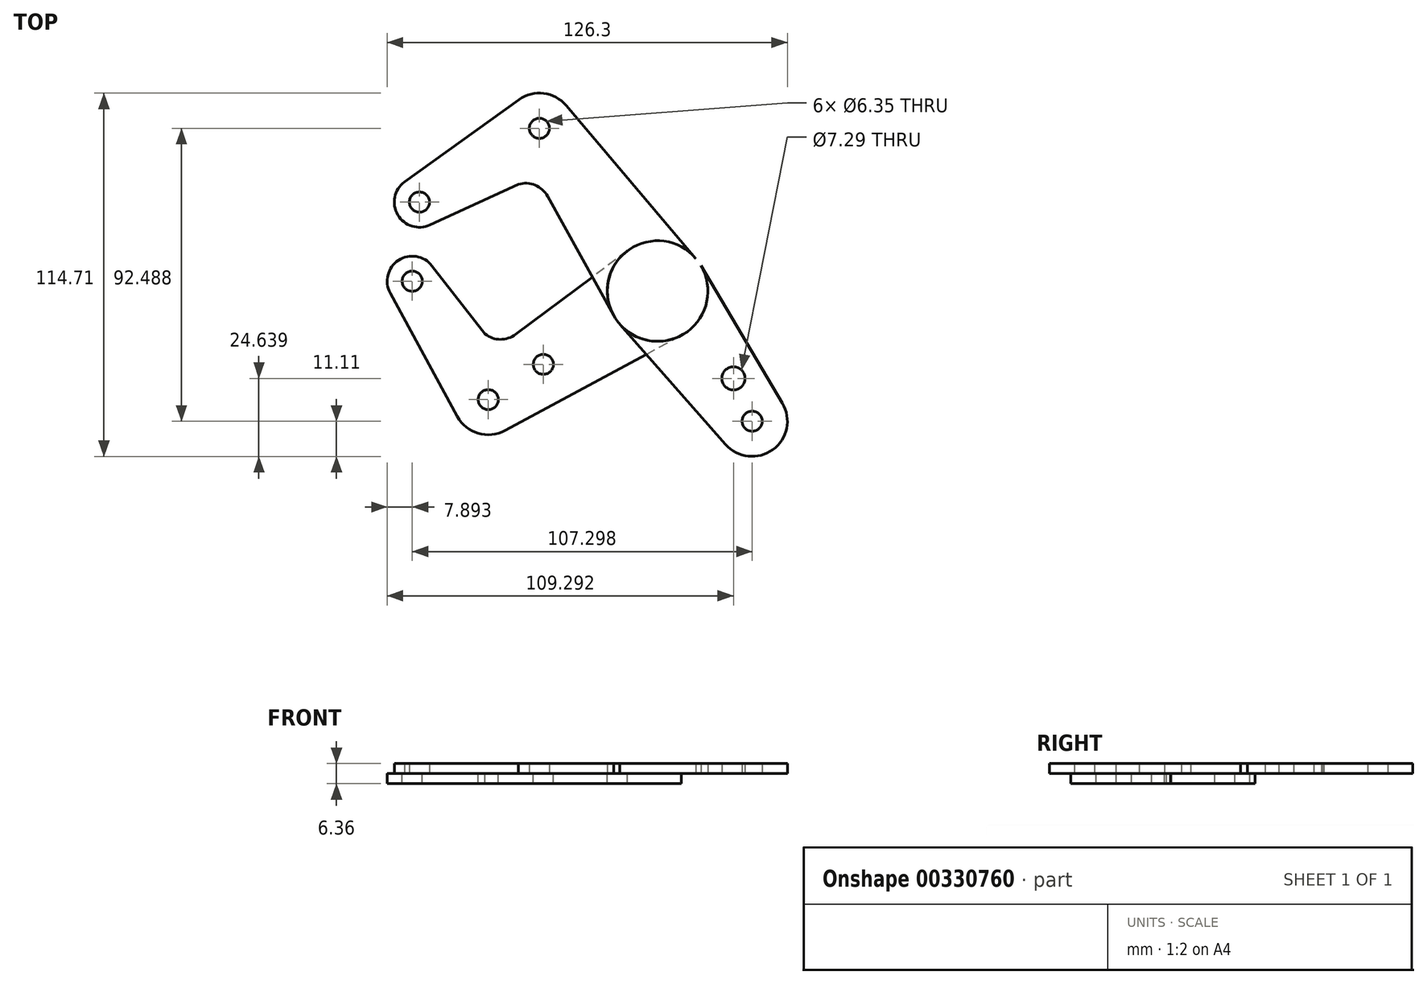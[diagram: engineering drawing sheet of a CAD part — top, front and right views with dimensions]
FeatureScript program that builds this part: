
annotation { "Feature Type Name" : "Feature", "Feature Type Description" : "" }
export const myFeature = defineFeature(function(context is Context, id is Id, definition is map)
    precondition{}
    {
        {
            var Q0;
            Q0=qCreatedBy(makeId("Top.planeOp"),FACE);
            var sketch = newSketch(context, id + "F0", { "sketchPlane" : qUnion([Q0])});
            skCircle(sketch, "E0", {"center": v(-60.51, 26.65) * mm, "radius": 7.94 * mm});
            skLineSegment(sketch, "E1", {"start": v(-60.51, 26.65) * mm, "end": v(-22.66, 49.95) * mm, "construction": true});
            skLineSegment(sketch, "E2", {"start": v(-22.66, 49.95) * mm, "end": v(51.96, -52.82) * mm, "construction": true});
            skCircle(sketch, "E3", {"center": v(-60.51, 26.65) * mm, "radius": 3.18 * mm});
            skCircle(sketch, "E4", {"center": v(14.65, -1.43) * mm, "radius": 15.88 * mm});
            skCircle(sketch, "E5", {"center": v(-22.66, 49.95) * mm, "radius": 11.11 * mm});
            skCircle(sketch, "E6", {"center": v(44.5, -42.54) * mm, "radius": 11.11 * mm});
            skCircle(sketch, "E7", {"center": v(44.5, -42.54) * mm, "radius": 3.18 * mm});
            skCircle(sketch, "E8", {"center": v(14.65, -1.43) * mm, "radius": 3.98 * mm});
            skCircle(sketch, "E9", {"center": v(38.6, -29.01) * mm, "radius": 3.65 * mm});
            skCircle(sketch, "E10", {"center": v(-22.66, 49.95) * mm, "radius": 3.18 * mm});
            skPoint(sketch, "E11", {"position": v(34.98, -29.43) * mm});
            skLineSegment(sketch, "E12", {"start": v(-57.2, 19.44) * mm, "end": v(-29.26, 32.28) * mm});
            skLineSegment(sketch, "E13", {"start": v(0.76, -9.12) * mm, "end": v(-20.07, 28.5) * mm});
            skLineSegment(sketch, "E14", {"start": v(-14.18, 57.13) * mm, "end": v(26.76, 8.83) * mm});
            skLineSegment(sketch, "E15", {"start": v(2.74, -11.92) * mm, "end": v(36.16, -49.88) * mm});
            skLineSegment(sketch, "E16", {"start": v(28.32, 6.65) * mm, "end": v(54.07, -36.88) * mm});
            skArc(sketch, "E17", {"start": v(-20.07, 28.5) * mm, "mid": v(-24, 32) * mm, "end": v(-29.26, 32.28) * mm});
            skLineSegment(sketch, "E18", {"start": v(-65.24, 33.03) * mm, "end": v(-29.15, 58.97) * mm});
            skCircle(sketch, "E19", {"center": v(14.65, -1.43) * mm, "radius": 3.18 * mm});
            skLineSegment(sketch, "E20", {"start": v(14.65, -1.43) * mm, "end": v(-38.8, -35.73) * mm, "construction": true});
            skLineSegment(sketch, "E21", {"start": v(-38.8, -35.73) * mm, "end": v(-62.8, 1.68) * mm, "construction": true});
            skCircle(sketch, "E22", {"center": v(-38.8, -35.73) * mm, "radius": 11.11 * mm});
            skCircle(sketch, "E23", {"center": v(-62.8, 1.68) * mm, "radius": 7.9 * mm});
            skCircle(sketch, "E24", {"center": v(-62.8, 1.68) * mm, "radius": 3.18 * mm});
            skCircle(sketch, "E25", {"center": v(-38.8, -35.73) * mm, "radius": 3.18 * mm});
            skLineSegment(sketch, "E26", {"start": v(-69.73, -2.1) * mm, "end": v(-48.55, -41.04) * mm});
            skLineSegment(sketch, "E27", {"start": v(-33.5, -45.5) * mm, "end": v(22.2, -15.4) * mm});
            skCircle(sketch, "E28", {"center": v(-21.41, -24.58) * mm, "radius": 3.18 * mm});
            skLineSegment(sketch, "E29", {"start": v(5.15, 11.28) * mm, "end": v(-30.17, -15.11) * mm});
            skArc(sketch, "E30", {"start": v(-39.79, -15.04) * mm, "mid": v(-35, -16.7) * mm, "end": v(-30.17, -15.11) * mm});
            skLineSegment(sketch, "E31", {"start": v(-56.56, 6.53) * mm, "end": v(-39.79, -15.04) * mm});
            skSolve(sketch);
        }
        {
            var Q0;
            {var subQ8=sQuery(id+"F0.wireOp",EDGE,"E12");Q0=makeQuery(id+"F0.imprint","IMPRINT",FACE,{"disambiguationData":[TD([[makeQuery(id+"F0.imprint","IMPRINT",EDGE,{"derivedFrom":subQ8}),1.0]])]});}
            var Q1;
            {var subQ0=sQuery(id+"F0.wireOp",EDGE,"E9");Q1=makeQuery(id+"F0.imprint","IMPRINT",FACE,{"disambiguationData":[TD([[makeQuery(id+"F0.imprint","IMPRINT",EDGE,{"derivedFrom":subQ0}),-1.0]])]});}
            var Q2;
            Q2=makeQuery(id+"F0.imprint","IMPRINT",FACE,{"disambiguationData":[TD([[makeQuery(id+"F0.imprint","IMPRINT",EDGE,{"derivedFrom":sQuery(id+"F0.wireOp",EDGE,"E8")}),-1.0]])]});
            var Q3;
            Q3=makeQuery(id+"F0.imprint","IMPRINT",FACE,{"disambiguationData":[TD([[makeQuery(id+"F0.imprint","IMPRINT",EDGE,{"derivedFrom":sQuery(id+"F0.wireOp",EDGE,"E7")}),-1.0]])]});
            var Q4;
            {var subQ0=sQuery(id+"F0.wireOp",EDGE,"E4");var subQ1=sQuery(id+"F0.wireOp",EDGE,"E13");var subQ2=makeQuery(id+"F0.imprint","INTERSECT",VERTEX,{"derivedFrom":[subQ1,subQ0]});Q4=makeQuery(id+"F0.imprint","IMPRINT",FACE,{"disambiguationData":[TD([[makeQuery(id+"F0.imprint","IMPRINT",EDGE,{"disambiguationData":[TD([[subQ2,-1.0]])],"derivedFrom":subQ1}),-1.0]])]});}
            var Q5;
            {var subQ0=sQuery(id+"F0.wireOp",EDGE,"E4");var subQ1=sQuery(id+"F0.wireOp",EDGE,"E15");var subQ2=makeQuery(id+"F0.imprint","INTERSECT",VERTEX,{"derivedFrom":[subQ1,subQ0]});Q5=makeQuery(id+"F0.imprint","IMPRINT",FACE,{"disambiguationData":[TD([[makeQuery(id+"F0.imprint","IMPRINT",EDGE,{"disambiguationData":[TD([[subQ2,-1.0]])],"derivedFrom":subQ1}),1.0]])]});}
            var Q6;
            Q6=makeQuery(id+"F0.imprint","IMPRINT",FACE,{"disambiguationData":[TD([[makeQuery(id+"F0.imprint","IMPRINT",EDGE,{"derivedFrom":sQuery(id+"F0.wireOp",EDGE,"E10")}),-1.0]])]});
            var Q7;
            Q7=makeQuery(id+"F0.imprint","IMPRINT",FACE,{"disambiguationData":[TD([[makeQuery(id+"F0.imprint","IMPRINT",EDGE,{"derivedFrom":sQuery(id+"F0.wireOp",EDGE,"E3")}),-1.0]])]});
            var Q8;
            Q8 = qSketchRegion(id + "F4", true);
            extrude(context, id + "F1", {"entities" : qUnion([Q0, Q1, Q2, Q3, Q4, Q5, Q6, Q7, Q8]), "depth" : 3.17 * mm});
        }
        {
            var Q0;
            {var subQ1=sQuery(id+"F0.wireOp",EDGE,"E26");Q0=makeQuery(id+"F0.imprint","IMPRINT",FACE,{"disambiguationData":[TD([[makeQuery(id+"F0.imprint","IMPRINT",EDGE,{"derivedFrom":subQ1}),1.0]])]});}
            var Q1;
            Q1=makeQuery(id+"F0.imprint","IMPRINT",FACE,{"disambiguationData":[TD([[makeQuery(id+"F0.imprint","IMPRINT",EDGE,{"derivedFrom":sQuery(id+"F0.wireOp",EDGE,"E24")}),-1.0]])]});
            var Q2;
            Q2=makeQuery(id+"F0.imprint","IMPRINT",FACE,{"disambiguationData":[TD([[makeQuery(id+"F0.imprint","IMPRINT",EDGE,{"derivedFrom":sQuery(id+"F0.wireOp",EDGE,"E25")}),-1.0]])]});
            var Q3;
            {var subQ0=sQuery(id+"F0.wireOp",EDGE,"E4");var subQ1=sQuery(id+"F0.wireOp",EDGE,"E13");var subQ2=makeQuery(id+"F0.imprint","INTERSECT",VERTEX,{"derivedFrom":[subQ1,subQ0]});Q3=makeQuery(id+"F0.imprint","IMPRINT",FACE,{"disambiguationData":[TD([[makeQuery(id+"F0.imprint","IMPRINT",EDGE,{"disambiguationData":[TD([[subQ2,-1.0]])],"derivedFrom":subQ1}),-1.0]])]});}
            var Q4;
            {var subQ0=sQuery(id+"F0.wireOp",EDGE,"E4");var subQ1=sQuery(id+"F0.wireOp",EDGE,"E15");var subQ2=makeQuery(id+"F0.imprint","INTERSECT",VERTEX,{"derivedFrom":[subQ1,subQ0]});Q4=makeQuery(id+"F0.imprint","IMPRINT",FACE,{"disambiguationData":[TD([[makeQuery(id+"F0.imprint","IMPRINT",EDGE,{"disambiguationData":[TD([[subQ2,-1.0]])],"derivedFrom":subQ1}),1.0]])]});}
            var Q5;
            Q5=makeQuery(id+"F0.imprint","IMPRINT",FACE,{"disambiguationData":[TD([[makeQuery(id+"F0.imprint","IMPRINT",EDGE,{"derivedFrom":sQuery(id+"F0.wireOp",EDGE,"E8")}),-1.0]])]});
            extrude(context, id + "F2", {"entities" : qUnion([Q0, Q1, Q2, Q3, Q4, Q5]), "oppositeDirection" : true, "depth" : 3.17 * mm});
        }
        {
            var Q0;
            Q0=makeQuery(id+"F1.opExtrude","CAP_FACE",FACE,{"disambiguationData":[OSD([sQuery(id+"F0.wireOp",EDGE,"E0"),sQuery(id+"F0.wireOp",EDGE,"E3"),sQuery(id+"F0.wireOp",EDGE,"E5"),sQuery(id+"F0.wireOp",EDGE,"E6"),sQuery(id+"F0.wireOp",EDGE,"E7"),sQuery(id+"F0.wireOp",EDGE,"E9"),sQuery(id+"F0.wireOp",EDGE,"E10"),sQuery(id+"F0.wireOp",EDGE,"E12"),sQuery(id+"F0.wireOp",EDGE,"E13"),sQuery(id+"F0.wireOp",EDGE,"E14"),sQuery(id+"F0.wireOp",EDGE,"E15"),sQuery(id+"F0.wireOp",EDGE,"E16"),sQuery(id+"F0.wireOp",EDGE,"E17"),sQuery(id+"F0.wireOp",EDGE,"E18"),sQuery(id+"F0.wireOp",EDGE,"E4"),sQuery(id+"F0.wireOp",EDGE,"E8")])],"isStart":false});
            var sketch = newSketch(context, id + "F3", { "sketchPlane" : qUnion([Q0])});
            skCircle(sketch, "E32", {"center": v(-22.66, 49.95) * mm, "radius": 3.98 * mm});
            skCircle(sketch, "E33", {"center": v(14.65, -1.43) * mm, "radius": 3.98 * mm});
            skCircle(sketch, "E34", {"center": v(44.5, -42.54) * mm, "radius": 11.11 * mm});
            skSolve(sketch);
        }
        {
            var Q0;
            Q0=makeQuery(id+"F2.opExtrude","CAP_FACE",FACE,{"disambiguationData":[OSD([sQuery(id+"F0.wireOp",EDGE,"E4"),sQuery(id+"F0.wireOp",EDGE,"E22"),sQuery(id+"F0.wireOp",EDGE,"E23"),sQuery(id+"F0.wireOp",EDGE,"E24"),sQuery(id+"F0.wireOp",EDGE,"E25"),sQuery(id+"F0.wireOp",EDGE,"E26"),sQuery(id+"F0.wireOp",EDGE,"E27"),sQuery(id+"F0.wireOp",EDGE,"E28"),sQuery(id+"F0.wireOp",EDGE,"E29"),sQuery(id+"F0.wireOp",EDGE,"E30"),sQuery(id+"F0.wireOp",EDGE,"E31"),sQuery(id+"F0.wireOp",EDGE,"E8")])],"isStart":false});
            var sketch = newSketch(context, id + "F4", { "sketchPlane" : qUnion([Q0])});
            skCircle(sketch, "E35", {"center": v(-62.8, -1.68) * mm, "radius": 3.18 * mm});
            skArc(sketch, "E36", {"start": v(-33.2, 45.34) * mm, "mid": v(-49.87, 34.82) * mm, "end": v(-31.72, 27.16) * mm});
            skLineSegment(sketch, "E37", {"start": v(-38.8, 35.73) * mm, "end": v(44.5, 42.54) * mm, "construction": true});
            skLineSegment(sketch, "E38", {"start": v(-31.72, 27.16) * mm, "end": v(-33.2, 45.34) * mm});
            skSolve(sketch);
        }
    });
